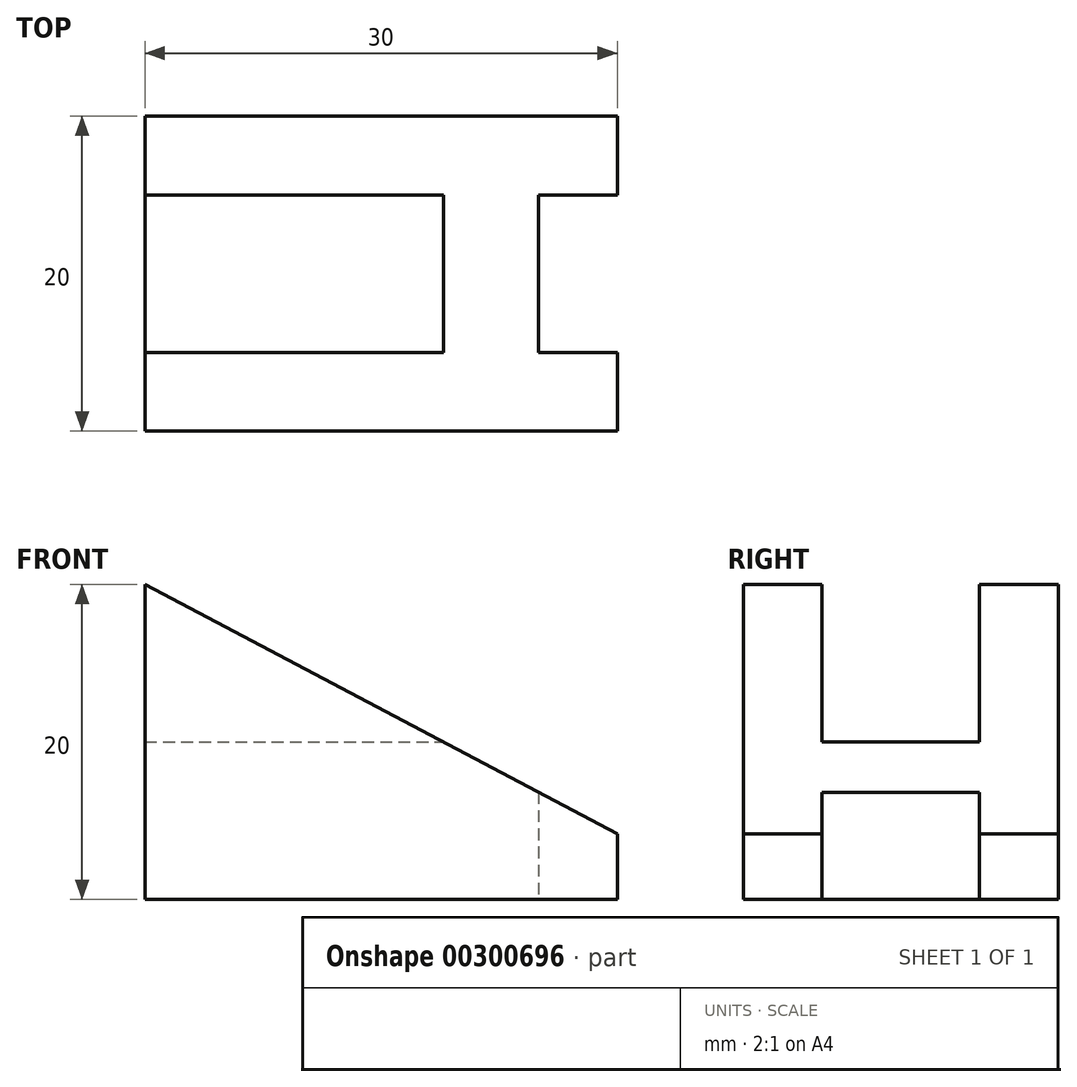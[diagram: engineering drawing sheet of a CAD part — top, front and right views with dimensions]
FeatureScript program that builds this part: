
annotation { "Feature Type Name" : "Feature", "Feature Type Description" : "" }
export const myFeature = defineFeature(function(context is Context, id is Id, definition is map)
    precondition{}
    {
        {
            var Q0;
            Q0=qCreatedBy(makeId("Front.planeOp"),FACE);
            var sketch = newSketch(context, id + "F0", { "sketchPlane" : qUnion([Q0])});
            skLineSegment(sketch, "E0", {"start": v(-30, 20) * mm, "end": v(-30, 0) * mm});
            skLineSegment(sketch, "E1", {"start": v(-30, 0) * mm, "end": v(0, 0) * mm});
            skLineSegment(sketch, "E2", {"start": v(0, 0) * mm, "end": v(0, 4.17) * mm});
            skLineSegment(sketch, "E3", {"start": v(0, 4.17) * mm, "end": v(-30, 20) * mm});
            skSolve(sketch);
        }
        {
            var Q0;
            Q0 = qSketchRegion(id + "F0", true);
            extrude(context, id + "F1", {"entities" : qUnion([Q0]), "depth" : 20 * mm});
        }
        {
            var Q0;
            Q0=qCreatedBy(makeId("Right.planeOp"),FACE);
            var sketch = newSketch(context, id + "F2", { "sketchPlane" : qUnion([Q0])});
            skLineSegment(sketch, "E4", {"start": v(-5, 20) * mm, "end": v(-5, 10) * mm});
            skLineSegment(sketch, "E5", {"start": v(-5, 10) * mm, "end": v(-15, 10) * mm});
            skLineSegment(sketch, "E6", {"start": v(-15, 10) * mm, "end": v(-15, 20) * mm});
            skLineSegment(sketch, "E7", {"start": v(-15, 20) * mm, "end": v(-5, 20) * mm});
            skSolve(sketch);
        }
        {
            var Q0;
            Q0 = qSketchRegion(id + "F2", true);
            extrude(context, id + "F3", {"entities" : qUnion([Q0]), "operationType" : NewBodyOperationType.REMOVE, "endBound" : BoundingType.THROUGH_ALL, "oppositeDirection" : true, "depth" : 15 * mm});
        }
        {
            var Q0;
            Q0=makeQuery(id+"F1.opExtrude","SWEPT_FACE",FACE,{"disambiguationData":[OSD([sQuery(id+"F0.wireOp",EDGE,"E1")])]});
            var sketch = newSketch(context, id + "F4", { "sketchPlane" : qUnion([Q0])});
            skLineSegment(sketch, "E8", {"start": v(0, 15) * mm, "end": v(-5, 15) * mm});
            skLineSegment(sketch, "E9", {"start": v(-5, 15) * mm, "end": v(-5, 5) * mm});
            skLineSegment(sketch, "E10", {"start": v(-5, 5) * mm, "end": v(0, 5) * mm});
            skSolve(sketch);
        }
        {
            var Q0;
            {var subQ0=sQuery(id+"F4.wireOp",EDGE,"E8");Q0=makeQuery(id+"F4.imprint","IMPRINT",FACE,{"disambiguationData":[TD([[makeQuery(id+"F4.imprint","IMPRINT",EDGE,{"derivedFrom":subQ0}),1.0]])]});}
            extrude(context, id + "F5", {"entities" : qUnion([Q0]), "operationType" : NewBodyOperationType.REMOVE, "oppositeDirection" : true, "depth" : 25 * mm});
        }
    });
